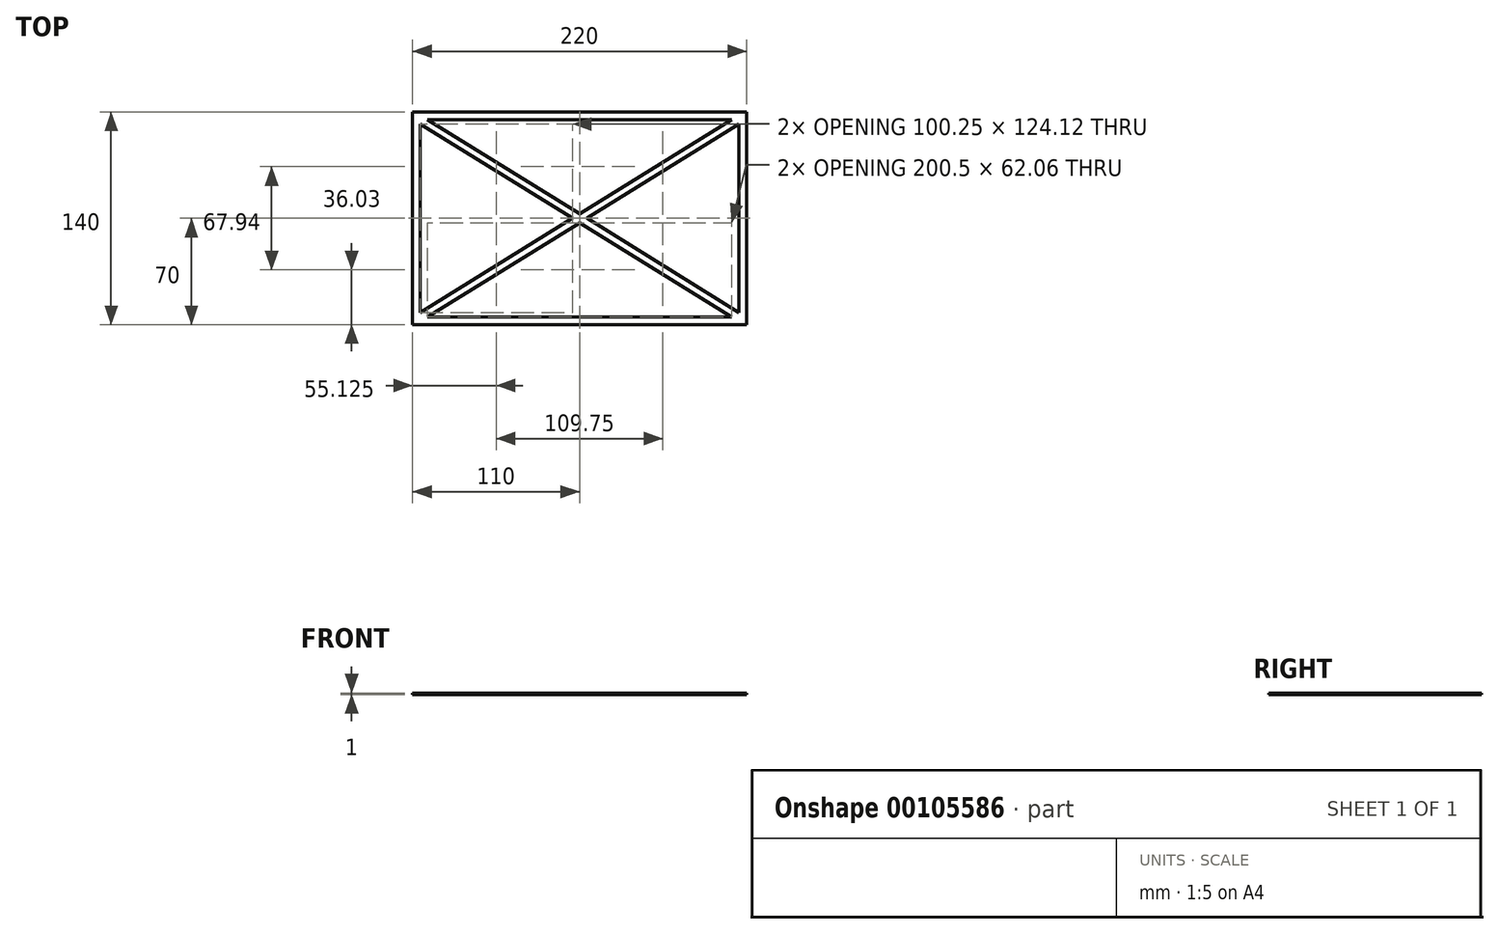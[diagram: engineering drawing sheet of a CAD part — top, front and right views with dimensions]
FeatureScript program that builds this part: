
annotation { "Feature Type Name" : "Feature", "Feature Type Description" : "" }
export const myFeature = defineFeature(function(context is Context, id is Id, definition is map)
    precondition{}
    {
        {
            var Q0;
            Q0=qCreatedBy(makeId("Top.planeOp"),FACE);
            var sketch = newSketch(context, id + "F0", { "sketchPlane" : qUnion([Q0])});
            skLineSegment(sketch, "E0.bottom", {"start": v(110, -70) * mm, "end": v(-110, -70) * mm});
            skLineSegment(sketch, "E0.top", {"start": v(110, 70) * mm, "end": v(-110, 70) * mm});
            skLineSegment(sketch, "E0.left", {"start": v(110, -70) * mm, "end": v(110, 70) * mm});
            skLineSegment(sketch, "E0.right", {"start": v(-110, -70) * mm, "end": v(-110, 70) * mm});
            skPoint(sketch, "E0.middle", {"position": v(0, 0) * mm});
            skLineSegment(sketch, "E1.0", {"start": v(-105, -62.06) * mm, "end": v(-105, 62.06) * mm});
            skLineSegment(sketch, "E1.1", {"start": v(100.25, -65) * mm, "end": v(-100.25, -65) * mm});
            skLineSegment(sketch, "E1.2", {"start": v(105, -62.06) * mm, "end": v(105, 62.06) * mm});
            skLineSegment(sketch, "E1.3", {"start": v(100.25, 65) * mm, "end": v(-100.25, 65) * mm});
            skLineSegment(sketch, "E2.0", {"start": v(-105, 62.06) * mm, "end": v(-4.75, 0) * mm});
            skLineSegment(sketch, "E3.0", {"start": v(-100.25, 65) * mm, "end": v(0, 2.94) * mm});
            skLineSegment(sketch, "E4.0", {"start": v(-100.25, -65) * mm, "end": v(0, -2.94) * mm});
            skLineSegment(sketch, "E5.0", {"start": v(-105, -62.06) * mm, "end": v(-4.75, 0) * mm});
            skLineSegment(sketch, "E6.trimOffspring", {"start": v(0, 2.94) * mm, "end": v(100.25, 65) * mm});
            skLineSegment(sketch, "E7.trimOffspring", {"start": v(0, -2.94) * mm, "end": v(100.25, -65) * mm});
            skLineSegment(sketch, "E8.trimOffspring", {"start": v(4.75, 0) * mm, "end": v(105, 62.06) * mm});
            skLineSegment(sketch, "E9.trimOffspring", {"start": v(4.75, 0) * mm, "end": v(105, -62.06) * mm});
            skSolve(sketch);
        }
        {
            var Q0;
            Q0=makeQuery(id+"F0.imprint","IMPRINT",FACE,{"disambiguationData":[TD([[makeQuery(id+"F0.imprint","IMPRINT",EDGE,{"derivedFrom":sQuery(id+"F0.wireOp",EDGE,"E0.bottom")}),-1.0]])]});
            extrude(context, id + "F1", {"entities" : qUnion([Q0]), "depth" : 1 * mm});
        }
    });
